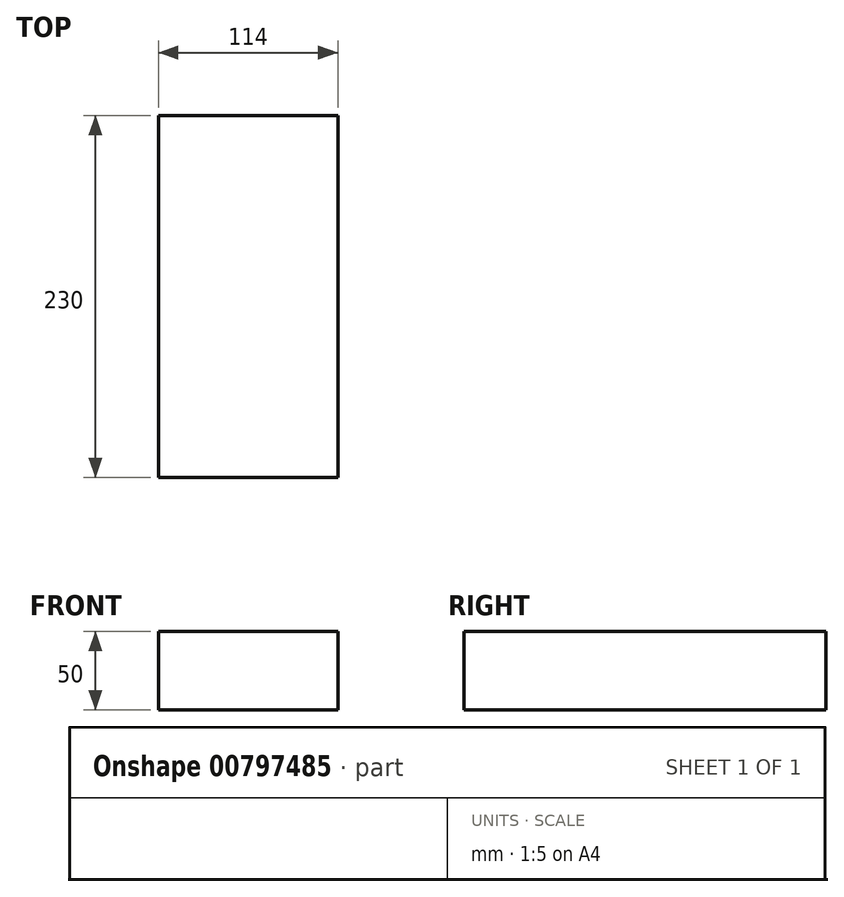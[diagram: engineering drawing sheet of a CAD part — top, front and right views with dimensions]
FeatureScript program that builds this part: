
annotation { "Feature Type Name" : "Feature", "Feature Type Description" : "" }
export const myFeature = defineFeature(function(context is Context, id is Id, definition is map)
    precondition{}
    {
        {
            var Q0;
            Q0=qCreatedBy(makeId("Front.planeOp"),FACE);
            var sketch = newSketch(context, id + "F0", { "sketchPlane" : qUnion([Q0])});
            skLineSegment(sketch, "E0.bottom", {"start": v(13.31, 0) * mm, "end": v(127.31, 0) * mm});
            skLineSegment(sketch, "E0.top", {"start": v(13.31, 50) * mm, "end": v(127.31, 50) * mm});
            skLineSegment(sketch, "E0.left", {"start": v(13.31, 0) * mm, "end": v(13.31, 50) * mm});
            skLineSegment(sketch, "E0.right", {"start": v(127.31, 0) * mm, "end": v(127.31, 50) * mm});
            skSolve(sketch);
        }
        {
            var Q0;
            Q0=makeQuery(id+"F0.imprint","IMPRINT",FACE,{"disambiguationData":[TD([[makeQuery(id+"F0.imprint","IMPRINT",EDGE,{"derivedFrom":sQuery(id+"F0.wireOp",EDGE,"E0.bottom")}),1.0]])]});
            extrude(context, id + "F1", {"entities" : qUnion([Q0]), "oppositeDirection" : true, "depth" : 230 * mm, "offsetDistance" : 25 * mm});
        }
    });
